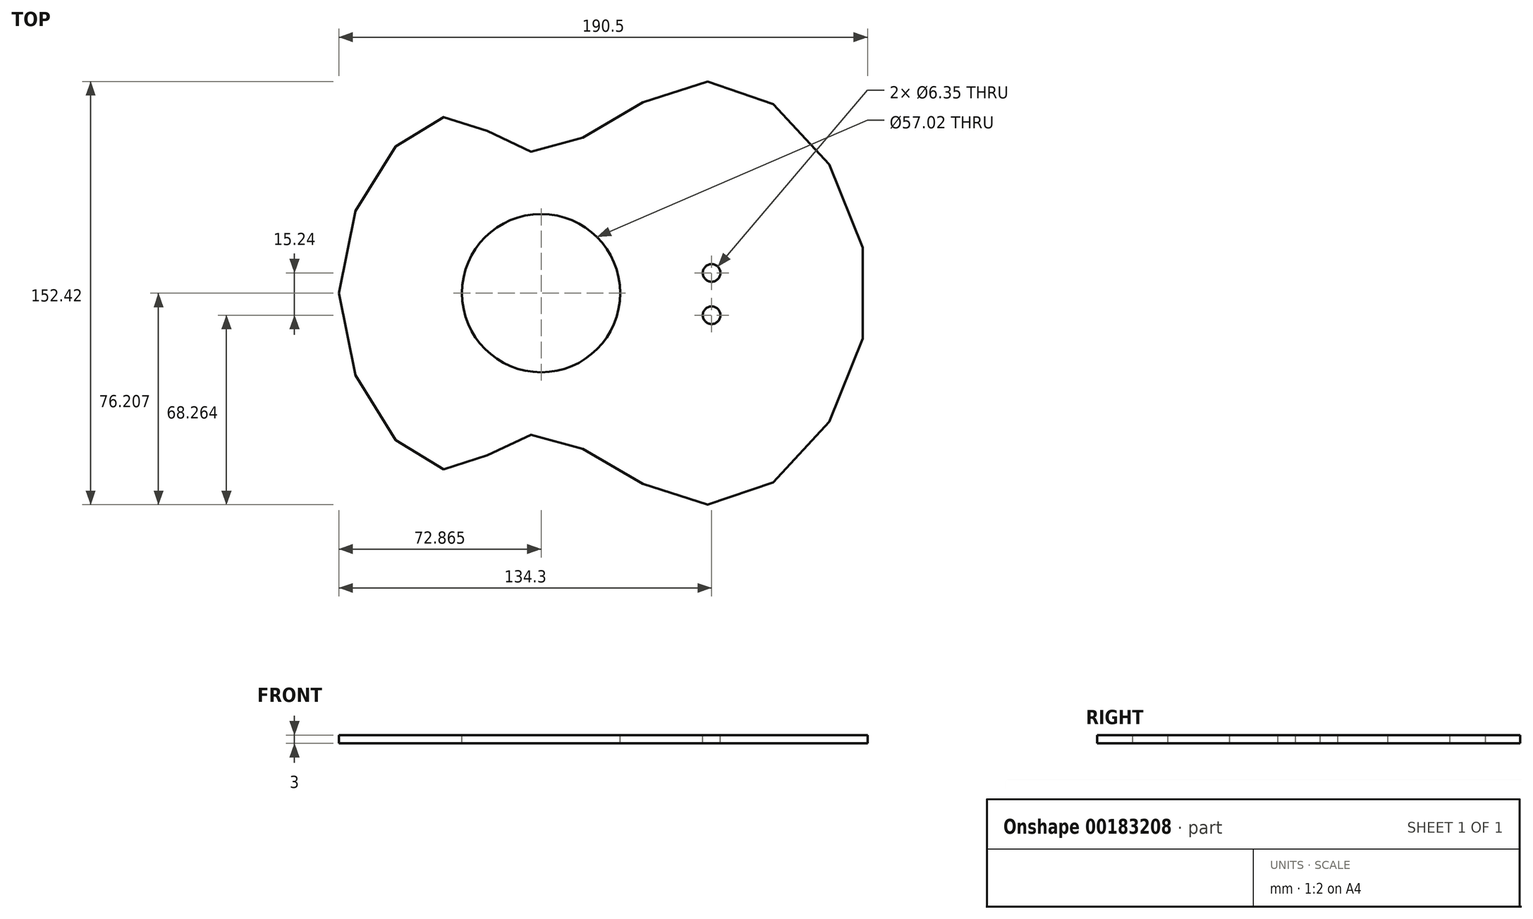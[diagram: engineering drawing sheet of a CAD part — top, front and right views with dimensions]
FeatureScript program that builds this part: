
annotation { "Feature Type Name" : "Feature", "Feature Type Description" : "" }
export const myFeature = defineFeature(function(context is Context, id is Id, definition is map)
    precondition{}
    {
        {
            var Q0;
            Q0=qCreatedBy(makeId("Top.planeOp"),FACE);
            var sketch = newSketch(context, id + "F0", { "sketchPlane" : qUnion([Q0])});
            skLineSegment(sketch, "E0", {"start": v(-154.7, -54.35) * mm, "end": v(35.8, -54.35) * mm, "construction": true});
            skLineSegment(sketch, "E1", {"start": v(-20.3, -54.35) * mm, "end": v(-20.3, 21.85) * mm, "construction": true});
            skLineSegment(sketch, "E2", {"start": v(-20.3, -54.35) * mm, "end": v(-20.3, -130.55) * mm, "construction": true});
            skLineSegment(sketch, "E3", {"start": v(-82.65, -54.35) * mm, "end": v(-82.65, -3.55) * mm, "construction": true});
            skLineSegment(sketch, "E4", {"start": v(-82.65, -54.35) * mm, "end": v(-82.65, -105.15) * mm, "construction": true});
            skLineSegment(sketch, "E5", {"start": v(-116.22, -54.35) * mm, "end": v(-116.22, 9.15) * mm, "construction": true});
            skLineSegment(sketch, "E6", {"start": v(-116.22, -54.35) * mm, "end": v(-116.22, -117.85) * mm, "construction": true});
            skFitSpline(sketch, "E7", {"points": [v(-154.7, -54.35) * mm, v(-116.22, 9.15) * mm, v(-82.65, -3.55) * mm, v(-20.3, 21.85) * mm, v(35.8, -54.35) * mm, v(-20.3, -130.55) * mm, v(-82.65, -105.15) * mm, v(-116.22, -117.85) * mm, v(-154.7, -54.35) * mm]});
            skSolve(sketch);
        }
        {
            var Q0;
            Q0=makeQuery(id+"F0.imprint","IMPRINT",FACE,{"disambiguationData":[TD([[makeQuery(id+"F0.imprint","IMPRINT",EDGE,{"derivedFrom":sQuery(id+"F0.wireOp",EDGE,"E7")}),-1.0]])]});
            var Q1;
            Q1=sQuery(id+"F0.wireOp",EDGE,"E7");
            extrude(context, id + "F1", {"entities" : qUnion([Q0]), "surfaceEntities" : qUnion([Q1]), "depth" : 3 * mm});
        }
        {
            var Q0;
            Q0=makeQuery(id+"F1.opExtrude","CAP_FACE",FACE,{"disambiguationData":[OSD([sQuery(id+"F0.wireOp",EDGE,"E7")])],"isStart":false});
            var sketch = newSketch(context, id + "F2", { "sketchPlane" : qUnion([Q0])});
            skLineSegment(sketch, "E8", {"start": v(-81.82, -3.53) * mm, "end": v(-81.82, -105.18) * mm, "construction": true});
            skLineSegment(sketch, "E9", {"start": v(-81.82, -105.18) * mm, "end": v(-81.82, -54.35) * mm, "construction": true});
            skCircle(sketch, "E10", {"center": v(-81.82, -54.35) * mm, "radius": 28.51 * mm});
            skSolve(sketch);
        }
        {
            var Q0;
            Q0 = qSketchRegion(id + "F2", true);
            extrude(context, id + "F3", {"entities" : qUnion([Q0]), "operationType" : NewBodyOperationType.REMOVE, "oppositeDirection" : true, "depth" : 3 * mm});
        }
        {
            var Q0;
            Q0=makeQuery(id+"F1.opExtrude","CAP_FACE",FACE,{"disambiguationData":[OSD([sQuery(id+"F0.wireOp",EDGE,"E7")])],"isStart":false});
            var sketch = newSketch(context, id + "F4", { "sketchPlane" : qUnion([Q0])});
            skLineSegment(sketch, "E11", {"start": v(-53.31, -54.68) * mm, "end": v(35.8, -54.68) * mm, "construction": true});
            skLineSegment(sketch, "E12", {"start": v(35.8, -54.68) * mm, "end": v(-53.31, -54.68) * mm, "construction": true});
            skLineSegment(sketch, "E13", {"start": v(-20.39, -54.68) * mm, "end": v(-20.39, -47.06) * mm, "construction": true});
            skLineSegment(sketch, "E14", {"start": v(-20.39, -47.06) * mm, "end": v(-20.39, -62.3) * mm, "construction": true});
            skCircle(sketch, "E15", {"center": v(-20.39, -62.3) * mm, "radius": 3.18 * mm});
            skCircle(sketch, "E16", {"center": v(-20.39, -47.06) * mm, "radius": 3.18 * mm});
            skSolve(sketch);
        }
        {
            var Q0;
            Q0=makeQuery(id+"F4.imprint","IMPRINT",FACE,{"disambiguationData":[TD([[makeQuery(id+"F4.imprint","IMPRINT",EDGE,{"derivedFrom":sQuery(id+"F4.wireOp",EDGE,"E16")}),1.0]])]});
            var Q1;
            Q1=makeQuery(id+"F4.imprint","IMPRINT",FACE,{"disambiguationData":[TD([[makeQuery(id+"F4.imprint","IMPRINT",EDGE,{"derivedFrom":sQuery(id+"F4.wireOp",EDGE,"E15")}),1.0]])]});
            extrude(context, id + "F5", {"entities" : qUnion([Q0, Q1]), "operationType" : NewBodyOperationType.REMOVE, "oppositeDirection" : true, "depth" : 25.4 * mm});
        }
    });
